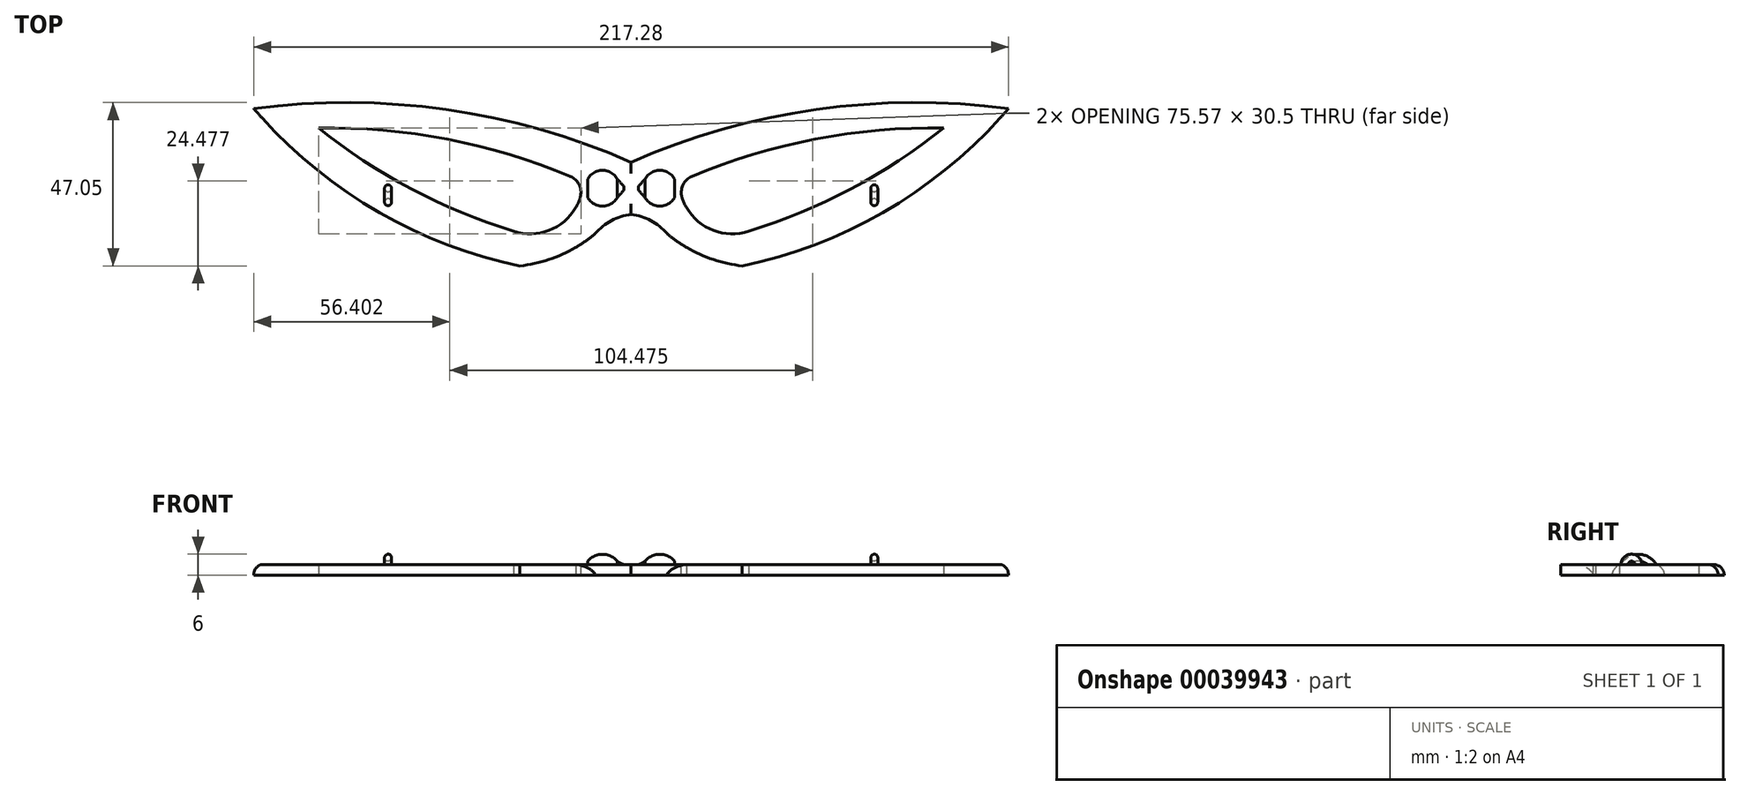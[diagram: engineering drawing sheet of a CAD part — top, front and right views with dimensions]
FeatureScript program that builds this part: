
annotation { "Feature Type Name" : "Feature", "Feature Type Description" : "" }
export const myFeature = defineFeature(function(context is Context, id is Id, definition is map)
    precondition{}
    {
        {
            var Q0;
            Q0=qCreatedBy(makeId("Top.planeOp"),FACE);
            var sketch = newSketch(context, id + "F0", { "sketchPlane" : qUnion([Q0])});
            skLineSegment(sketch, "E0", {"start": v(0, 7.5) * mm, "end": v(0, -7.5) * mm, "construction": true});
            skLineSegment(sketch, "E1", {"start": v(-32, 0) * mm, "end": v(32, 0) * mm, "construction": true});
            skCircle(sketch, "E2", {"center": v(-32, 0) * mm, "radius": 12.5 * mm, "construction": true});
            skLineSegment(sketch, "E3", {"start": v(-32, 0) * mm, "end": v(-108.64, 22.94) * mm, "construction": true});
            skArc(sketch, "E4", {"start": v(0, 7.5) * mm, "mid": v(-53.26, 22.66) * mm, "end": v(-108.64, 22.94) * mm});
            skArc(sketch, "E5", {"start": v(-108.64, 22.94) * mm, "mid": v(-74.07, -6.06) * mm, "end": v(-32, -22.36) * mm});
            skArc(sketch, "E6", {"start": v(-32, -22.36) * mm, "mid": v(-20.46, -19.3) * mm, "end": v(-10.3, -13.03) * mm});
            skArc(sketch, "E7", {"start": v(0, -7.5) * mm, "mid": v(-5.68, -9.3) * mm, "end": v(-10.3, -13.03) * mm});
            skArc(sketch, "E8", {"start": v(-90.02, 17.37) * mm, "mid": v(-63.35, -0.17) * mm, "end": v(-33.85, -12.36) * mm});
            skArc(sketch, "E9", {"start": v(-14.66, 2.23) * mm, "mid": v(-51.53, 13.85) * mm, "end": v(-90.02, 17.37) * mm});
            skArc(sketch, "E10", {"start": v(-15.93, -5.5) * mm, "mid": v(-14.48, -1.77) * mm, "end": v(-14.66, 2.23) * mm});
            skArc(sketch, "E11", {"start": v(-33.85, -12.36) * mm, "mid": v(-23.66, -12.14) * mm, "end": v(-15.93, -5.5) * mm});
            skArc(sketch, "E12.MirrorCS", {"start": v(0, 7.5) * mm, "mid": v(53.26, 22.66) * mm, "end": v(108.64, 22.94) * mm});
            skArc(sketch, "E13.MirrorCS", {"start": v(108.64, 22.94) * mm, "mid": v(74.07, -6.06) * mm, "end": v(32, -22.36) * mm});
            skArc(sketch, "E14.MirrorCS", {"start": v(32, -22.36) * mm, "mid": v(20.46, -19.3) * mm, "end": v(10.3, -13.03) * mm});
            skArc(sketch, "E15.MirrorCS", {"start": v(0, -7.5) * mm, "mid": v(5.68, -9.3) * mm, "end": v(10.3, -13.03) * mm});
            skArc(sketch, "E16.MirrorCS", {"start": v(14.66, 2.23) * mm, "mid": v(51.53, 13.85) * mm, "end": v(90.02, 17.37) * mm});
            skArc(sketch, "E17.MirrorCS", {"start": v(90.02, 17.37) * mm, "mid": v(63.35, -0.17) * mm, "end": v(33.85, -12.36) * mm});
            skArc(sketch, "E18.MirrorCS", {"start": v(33.85, -12.36) * mm, "mid": v(23.66, -12.14) * mm, "end": v(15.93, -5.5) * mm});
            skArc(sketch, "E19.MirrorCS", {"start": v(15.93, -5.5) * mm, "mid": v(14.48, -1.77) * mm, "end": v(14.66, 2.23) * mm});
            skSolve(sketch);
        }
        {
            var Q0;
            Q0 = qSketchRegion(id + "F0", true);
            extrude(context, id + "F1", {"entities" : qUnion([Q0]), "depth" : 3 * mm});
        }
        {
            var Q0;
            Q0=makeQuery(id+"F1.opExtrude","SWEPT_EDGE",EDGE,{"disambiguationData":[OSD([sQuery(id+"F0.wireOp",EDGE,"E9"),sQuery(id+"F0.wireOp",EDGE,"E10")])]});
            var Q1;
            Q1=makeQuery(id+"F1.opExtrude","SWEPT_EDGE",EDGE,{"disambiguationData":[OSD([sQuery(id+"F0.wireOp",EDGE,"E16.MirrorCS"),sQuery(id+"F0.wireOp",EDGE,"E19.MirrorCS")])]});
            fillet(context, id + "F2", {"entities" : qUnion([Q0, Q1]), "radius" : 5 * mm, "tangentPropagation" : true, "allowEdgeOverflow" : false});
        }
        {
            var Q0;
            Q0=makeQuery(id+"F1.opExtrude","CAP_FACE",FACE,{"disambiguationData":[OSD([sQuery(id+"F0.wireOp",EDGE,"E4"),sQuery(id+"F0.wireOp",EDGE,"E5"),sQuery(id+"F0.wireOp",EDGE,"E6"),sQuery(id+"F0.wireOp",EDGE,"E7"),sQuery(id+"F0.wireOp",EDGE,"E8"),sQuery(id+"F0.wireOp",EDGE,"E9"),sQuery(id+"F0.wireOp",EDGE,"E10"),sQuery(id+"F0.wireOp",EDGE,"E11"),sQuery(id+"F0.wireOp",EDGE,"E12.MirrorCS"),sQuery(id+"F0.wireOp",EDGE,"E13.MirrorCS"),sQuery(id+"F0.wireOp",EDGE,"E14.MirrorCS"),sQuery(id+"F0.wireOp",EDGE,"E15.MirrorCS"),sQuery(id+"F0.wireOp",EDGE,"E16.MirrorCS"),sQuery(id+"F0.wireOp",EDGE,"E17.MirrorCS"),sQuery(id+"F0.wireOp",EDGE,"E18.MirrorCS"),sQuery(id+"F0.wireOp",EDGE,"E19.MirrorCS")])],"isStart":false});
            var sketch = newSketch(context, id + "F3", { "sketchPlane" : qUnion([Q0])});
            skLineSegment(sketch, "E20", {"start": v(-70, 0) * mm, "end": v(70, 0) * mm, "construction": true});
            skLineSegment(sketch, "E21", {"start": v(-70, 0) * mm, "end": v(-70, -2) * mm, "construction": true});
            skCircle(sketch, "E22", {"center": v(-70, 0) * mm, "radius": 1 * mm});
            skLineSegment(sketch, "E23", {"start": v(-70, -2) * mm, "end": v(-74, -2) * mm, "construction": true});
            skPoint(sketch, "E24.endSnap0", {"position": v(0, 0) * mm});
            skLineSegment(sketch, "E25", {"start": v(0, 5) * mm, "end": v(0, -5) * mm, "construction": true});
            skCircle(sketch, "E26.MirrorC", {"center": v(70, 0) * mm, "radius": 1 * mm});
            skSolve(sketch);
        }
        {
            var Q0;
            Q0 = qSketchRegion(id + "F3", true);
            var Q1;
            Q1=sQuery(id+"F3.wireOp",EDGE,"E23");
            revolve(context, id + "F4", {"operationType" : NewBodyOperationType.ADD, "entities" : qUnion([Q0]), "axis" : qUnion([Q1]), "revolveType" : RevolveType.FULL});
        }
        {
            var Q0;
            Q0=qCreatedBy(makeId("Top.planeOp"),FACE);
            var sketch = newSketch(context, id + "F5", { "sketchPlane" : qUnion([Q0])});
            skLineSegment(sketch, "E27", {"start": v(-12.5, 0) * mm, "end": v(12.5, 0) * mm});
            skLineSegment(sketch, "E28", {"start": v(-12.5, 0) * mm, "end": v(-12.5, 4) * mm});
            skArc(sketch, "E29", {"start": v(-4, 4) * mm, "mid": v(-8.25, 5.97) * mm, "end": v(-12.5, 4) * mm});
            skLineSegment(sketch, "E30", {"start": v(0, 0) * mm, "end": v(0, 1.88) * mm, "construction": true});
            skArc(sketch, "E31.MirrorCS", {"start": v(4, 4) * mm, "mid": v(8.25, 5.97) * mm, "end": v(12.5, 4) * mm});
            skLineSegment(sketch, "E32.MirrorCS", {"start": v(12.5, 0) * mm, "end": v(12.5, 4) * mm});
            skArc(sketch, "E33", {"start": v(-4, 4) * mm, "mid": v(0, 2.68) * mm, "end": v(4, 4) * mm});
            skLineSegment(sketch, "E34", {"start": v(-4, 4) * mm, "end": v(4, 4) * mm, "construction": true});
            skSolve(sketch);
        }
        {
            var Q0;
            Q0=makeQuery(id+"F5.imprint","IMPRINT",FACE,{"disambiguationData":[TD([[makeQuery(id+"F5.imprint","IMPRINT",EDGE,{"derivedFrom":sQuery(id+"F5.wireOp",EDGE,"E27")}),1.0]])]});
            var Q1;
            Q1=sQuery(id+"F5.wireOp",EDGE,"E27");
            revolve(context, id + "F6", {"operationType" : NewBodyOperationType.ADD, "entities" : qUnion([Q0]), "axis" : qUnion([Q1]), "revolveType" : RevolveType.ONE_DIRECTION, "angle" : 180 * degree});
        }
        {
            var Q0;
            Q0=makeQuery(id+"F1.opExtrude","CAP_EDGE",EDGE,{"disambiguationData":[OSD([sQuery(id+"F0.wireOp",EDGE,"E7")])],"isStart":false});
            var Q1;
            Q1=makeQuery(id+"F1.opExtrude","CAP_EDGE",EDGE,{"disambiguationData":[OSD([sQuery(id+"F0.wireOp",EDGE,"E15.MirrorCS")])],"isStart":false});
            var Q2;
            Q2=makeQuery(id+"F1.opExtrude","CAP_EDGE",EDGE,{"disambiguationData":[OSD([sQuery(id+"F0.wireOp",EDGE,"E12.MirrorCS")])],"isStart":false});
            var Q3;
            Q3=makeQuery(id+"F1.opExtrude","CAP_EDGE",EDGE,{"disambiguationData":[OSD([sQuery(id+"F0.wireOp",EDGE,"E4")])],"isStart":false});
            fillet(context, id + "F7", {"entities" : qUnion([Q0, Q1, Q2, Q3]), "radius" : 3 * mm, "tangentPropagation" : true, "allowEdgeOverflow" : false});
        }
    });
